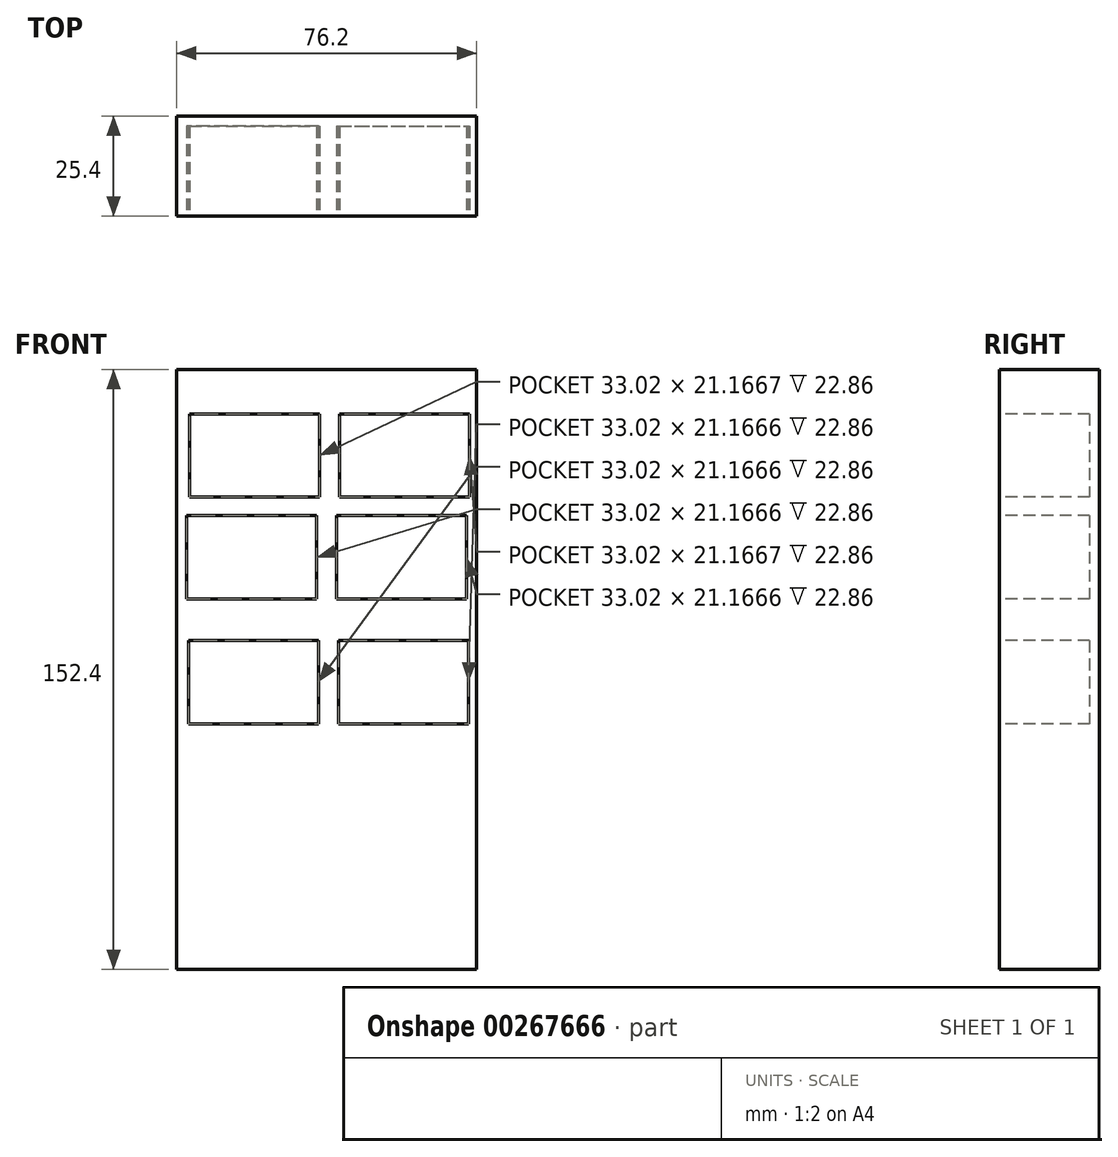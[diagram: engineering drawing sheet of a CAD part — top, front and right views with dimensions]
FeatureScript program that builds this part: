
annotation { "Feature Type Name" : "Feature", "Feature Type Description" : "" }
export const myFeature = defineFeature(function(context is Context, id is Id, definition is map)
    precondition{}
    {
        {
            var Q0;
            Q0=qCreatedBy(makeId("Front.planeOp"),FACE);
            var sketch = newSketch(context, id + "F0", { "sketchPlane" : qUnion([Q0])});
            skLineSegment(sketch, "E0.bottom", {"start": v(38.1, 76.2) * mm, "end": v(-38.1, 76.2) * mm});
            skLineSegment(sketch, "E0.top", {"start": v(38.1, -76.2) * mm, "end": v(-38.1, -76.2) * mm});
            skLineSegment(sketch, "E0.left", {"start": v(38.1, 76.2) * mm, "end": v(38.1, -76.2) * mm});
            skLineSegment(sketch, "E0.right", {"start": v(-38.1, 76.2) * mm, "end": v(-38.1, -76.2) * mm});
            skPoint(sketch, "E0.middle", {"position": v(0, 0) * mm});
            skSolve(sketch);
        }
        {
            var Q0;
            Q0=makeQuery(id+"F0.imprint","IMPRINT",FACE,{"disambiguationData":[TD([[makeQuery(id+"F0.imprint","IMPRINT",EDGE,{"derivedFrom":sQuery(id+"F0.wireOp",EDGE,"E0.bottom")}),1.0]])]});
            extrude(context, id + "F1", {"entities" : qUnion([Q0]), "depth" : 25.4 * mm});
        }
        {
            var Q0;
            Q0=makeQuery(id+"F1.opExtrude","CAP_FACE",FACE,{"disambiguationData":[OSD([sQuery(id+"F0.wireOp",EDGE,"E0.bottom"),sQuery(id+"F0.wireOp",EDGE,"E0.top"),sQuery(id+"F0.wireOp",EDGE,"E0.left"),sQuery(id+"F0.wireOp",EDGE,"E0.right")])],"isStart":false});
            var sketch = newSketch(context, id + "F2", { "sketchPlane" : qUnion([Q0])});
            skLineSegment(sketch, "E1.bottom", {"start": v(-34.79, 64.96) * mm, "end": v(-1.77, 64.96) * mm});
            skLineSegment(sketch, "E1.top", {"start": v(-34.79, 43.79) * mm, "end": v(-1.77, 43.79) * mm});
            skLineSegment(sketch, "E1.left", {"start": v(-34.79, 64.96) * mm, "end": v(-34.79, 43.79) * mm});
            skLineSegment(sketch, "E1.right", {"start": v(-1.77, 64.96) * mm, "end": v(-1.77, 43.79) * mm});
            skLineSegment(sketch, "E2.bottom", {"start": v(3.31, 64.96) * mm, "end": v(36.33, 64.96) * mm});
            skLineSegment(sketch, "E2.top", {"start": v(3.31, 43.79) * mm, "end": v(36.33, 43.79) * mm});
            skLineSegment(sketch, "E2.left", {"start": v(3.31, 64.96) * mm, "end": v(3.31, 43.79) * mm});
            skLineSegment(sketch, "E2.right", {"start": v(36.33, 64.96) * mm, "end": v(36.33, 43.79) * mm});
            skLineSegment(sketch, "E3.bottom", {"start": v(-2.54, 39.1) * mm, "end": v(-35.56, 39.1) * mm});
            skLineSegment(sketch, "E3.top", {"start": v(-2.54, 17.93) * mm, "end": v(-35.56, 17.93) * mm});
            skLineSegment(sketch, "E3.left", {"start": v(-2.54, 39.1) * mm, "end": v(-2.54, 17.93) * mm});
            skLineSegment(sketch, "E3.right", {"start": v(-35.56, 39.1) * mm, "end": v(-35.56, 17.93) * mm});
            skLineSegment(sketch, "E4.bottom", {"start": v(-2.06, 7.37) * mm, "end": v(-35.08, 7.37) * mm});
            skLineSegment(sketch, "E4.top", {"start": v(-2.06, -13.8) * mm, "end": v(-35.08, -13.8) * mm});
            skLineSegment(sketch, "E4.left", {"start": v(-2.06, 7.37) * mm, "end": v(-2.06, -13.8) * mm});
            skLineSegment(sketch, "E4.right", {"start": v(-35.08, 7.37) * mm, "end": v(-35.08, -13.8) * mm});
            skLineSegment(sketch, "E5.bottom", {"start": v(3.02, 7.37) * mm, "end": v(36.04, 7.37) * mm});
            skLineSegment(sketch, "E5.top", {"start": v(3.02, -13.8) * mm, "end": v(36.04, -13.8) * mm});
            skLineSegment(sketch, "E5.left", {"start": v(3.02, 7.37) * mm, "end": v(3.02, -13.8) * mm});
            skLineSegment(sketch, "E5.right", {"start": v(36.04, 7.37) * mm, "end": v(36.04, -13.8) * mm});
            skLineSegment(sketch, "E6.bottom", {"start": v(2.54, 39.1) * mm, "end": v(35.56, 39.1) * mm});
            skLineSegment(sketch, "E6.top", {"start": v(2.54, 17.93) * mm, "end": v(35.56, 17.93) * mm});
            skLineSegment(sketch, "E6.left", {"start": v(2.54, 39.1) * mm, "end": v(2.54, 17.93) * mm});
            skLineSegment(sketch, "E6.right", {"start": v(35.56, 39.1) * mm, "end": v(35.56, 17.93) * mm});
            skSolve(sketch);
        }
        {
            var Q0;
            Q0=makeQuery(id+"F2.imprint","IMPRINT",FACE,{"disambiguationData":[TD([[makeQuery(id+"F2.imprint","IMPRINT",EDGE,{"derivedFrom":sQuery(id+"F2.wireOp",EDGE,"E1.bottom")}),-1.0]])]});
            extrude(context, id + "F3", {"entities" : qUnion([Q0]), "operationType" : NewBodyOperationType.REMOVE, "oppositeDirection" : true, "depth" : 22.86 * mm});
        }
        {
            var Q0;
            Q0=makeQuery(id+"F2.imprint","IMPRINT",FACE,{"disambiguationData":[TD([[makeQuery(id+"F2.imprint","IMPRINT",EDGE,{"derivedFrom":sQuery(id+"F2.wireOp",EDGE,"E2.bottom")}),-1.0]])]});
            var Q1;
            Q1=makeQuery(id+"F2.imprint","IMPRINT",FACE,{"disambiguationData":[TD([[makeQuery(id+"F2.imprint","IMPRINT",EDGE,{"derivedFrom":sQuery(id+"F2.wireOp",EDGE,"e52KiWnv-5oNI-HAu1-27Uf-qFtm82sFJdFm.bottom")}),-1.0]])]});
            var Q2;
            Q2=makeQuery(id+"F2.imprint","IMPRINT",FACE,{"disambiguationData":[TD([[makeQuery(id+"F2.imprint","IMPRINT",EDGE,{"derivedFrom":sQuery(id+"F2.wireOp",EDGE,"E3.bottom")}),1.0]])]});
            var Q3;
            Q3=makeQuery(id+"F2.imprint","IMPRINT",FACE,{"disambiguationData":[TD([[makeQuery(id+"F2.imprint","IMPRINT",EDGE,{"derivedFrom":sQuery(id+"F2.wireOp",EDGE,"E4.bottom")}),1.0]])]});
            var Q4;
            Q4=makeQuery(id+"F2.imprint","IMPRINT",FACE,{"disambiguationData":[TD([[makeQuery(id+"F2.imprint","IMPRINT",EDGE,{"derivedFrom":sQuery(id+"F2.wireOp",EDGE,"E5.bottom")}),-1.0]])]});
            extrude(context, id + "F4", {"entities" : qUnion([Q0, Q1, Q2, Q3, Q4]), "operationType" : NewBodyOperationType.REMOVE, "oppositeDirection" : true, "depth" : 22.86 * mm});
        }
        {
            var Q0;
            Q0=makeQuery(id+"F2.imprint","IMPRINT",FACE,{"disambiguationData":[TD([[makeQuery(id+"F2.imprint","IMPRINT",EDGE,{"derivedFrom":sQuery(id+"F2.wireOp",EDGE,"E6.bottom")}),-1.0]])]});
            extrude(context, id + "F5", {"entities" : qUnion([Q0]), "operationType" : NewBodyOperationType.REMOVE, "oppositeDirection" : true, "depth" : 22.86 * mm});
        }
    });
